# Revit family: Table-Teknion-CQTHU_Partner_Table-R2020
name_source: partatom
category: Furniture
units: mm (PartAtom-declared; Revit-internal decimal feet)

## family parameters
Always vertical = Yes
Cut with Voids When Loaded = No
OmniClass Number = 23.40.20.00
OmniClass Title = General Furniture and Specialties
Room Calculation Point = No
Shared = Yes
Work Plane-Based = No

## types (6) — shared parameters
Assembly Code = E2020200
Manufacturer = Teknion
Manufacturer Fax = 416.661.4586
Part Number = CQTHU
Product Documentation Link = https://assets.teknion.com
Product Line = Routes Tables
Product Page URL = https://www.teknion.com
Series = Routes
Sustainability Data = https://www.teknion.com
URL = www.teknion.com
Unit Weight URL = http://www.teknion.com
Warranty = http://www.teknion.com
zero-valued in all types: Default Elevation

## per-type parameters (varying)
| type | Description | Fixed Leg | Height | Mobile Leg | Model | Support Leg | Support Surface |
| Bar Height, Fixed Mobility | Partner Table - Bar Height with Fixed Mobility | Yes | 42 " | No | CQTHUBF4272 | Yes | No |
| Task Height, Fixed Mobility | Partner Table - Task Height with Fixed Mobility | Yes | 29 " | No | CQTHUTF4272 | No | Yes |
| Counter Height, Fixed Mobility | Partner Table - Counter Height with Fixed Mobility | Yes | 36 " | No | CQTHUCF4272 | Yes | No |
| Bar Height, Mobile Mobility | Partner Table - Bar Height with Mobile Mobility | No | 42 " | Yes | CQTHUBM4272 | Yes | No |
| Counter Height, Mobile Mobility | Partner Table - Counter Height with Mobile Mobility | No | 36 " | Yes | CQTHUCM4272 | Yes | No |
| Task Height, Mobile Mobility | Partner Table - Task Height with Mobile Mobility | No | 29 " | Yes | CQTHUTM4272 | No | Yes |

## geometry (parser evidence)
native form markers: Sweep x4
no freeform markers — native parametric forms only
